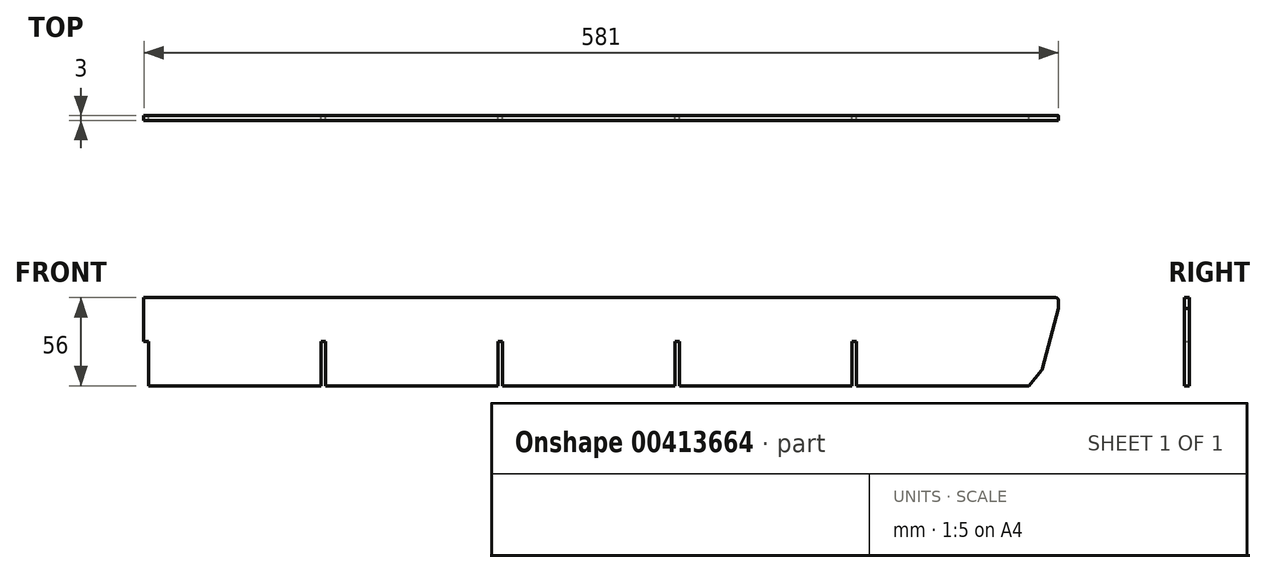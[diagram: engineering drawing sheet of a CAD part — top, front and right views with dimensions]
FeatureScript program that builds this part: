
annotation { "Feature Type Name" : "Feature", "Feature Type Description" : "" }
export const myFeature = defineFeature(function(context is Context, id is Id, definition is map)
    precondition{}
    {
        {
            var Q0;
            Q0=qCreatedBy(makeId("Front.planeOp"),FACE);
            var sketch = newSketch(context, id + "F0", { "sketchPlane" : qUnion([Q0])});
            skLineSegment(sketch, "E0.bottom", {"start": v(-12.6, -20.13) * mm, "end": v(-8.8, -20.13) * mm});
            skLineSegment(sketch, "E0.top", {"start": v(-12.6, 35.87) * mm, "end": v(345.4, 35.87) * mm});
            skLineSegment(sketch, "E0.right", {"start": v(347.4, 28.87) * mm, "end": v(347.4, 33.87) * mm});
            skArc(sketch, "E1", {"start": v(347.4, 33.87) * mm, "mid": v(346.82, 35.28) * mm, "end": v(345.4, 35.87) * mm});
            skLineSegment(sketch, "E2", {"start": v(328.4, -20.13) * mm, "end": v(336.6, -10.36) * mm});
            skPoint(sketch, "E3", {"position": v(347.4, 28.87) * mm});
            skLineSegment(sketch, "E4", {"start": v(347.4, 28.87) * mm, "end": v(337.2, -9.21) * mm});
            skArc(sketch, "E5", {"start": v(336.6, -10.36) * mm, "mid": v(336.97, -9.82) * mm, "end": v(337.2, -9.21) * mm});
            skLineSegment(sketch, "E6.MirrorCS", {"start": v(-12.6, 35.87) * mm, "end": v(-233.6, 35.87) * mm});
            skLineSegment(sketch, "E7.MirrorCS", {"start": v(-12.6, -20.13) * mm, "end": v(-118.2, -20.13) * mm});
            skPoint(sketch, "E8.orphan", {"position": v(347.4, -20.13) * mm});
            skLineSegment(sketch, "E9.top", {"start": v(216, 7.87) * mm, "end": v(219, 7.87) * mm});
            skLineSegment(sketch, "E9.left", {"start": v(216, -20.13) * mm, "end": v(216, 7.87) * mm});
            skLineSegment(sketch, "E9.right", {"start": v(219, -20.13) * mm, "end": v(219, 7.87) * mm});
            skLineSegment(sketch, "E10.bottom", {"start": v(-233.6, 7.87) * mm, "end": v(-230.6, 7.87) * mm});
            skLineSegment(sketch, "E10.left", {"start": v(-233.6, 7.87) * mm, "end": v(-233.6, -20.13) * mm});
            skLineSegment(sketch, "E10.right", {"start": v(-230.6, 7.87) * mm, "end": v(-230.6, -20.13) * mm});
            skLineSegment(sketch, "E11.bottom", {"start": v(103.6, 7.87) * mm, "end": v(106.6, 7.87) * mm});
            skLineSegment(sketch, "E11.left", {"start": v(103.6, 7.87) * mm, "end": v(103.6, -20.13) * mm});
            skLineSegment(sketch, "E11.right", {"start": v(106.6, 7.87) * mm, "end": v(106.6, -20.13) * mm});
            skLineSegment(sketch, "E12.bottom", {"start": v(-8.8, 7.87) * mm, "end": v(-5.8, 7.87) * mm});
            skLineSegment(sketch, "E12.left", {"start": v(-8.8, 7.87) * mm, "end": v(-8.8, -20.13) * mm});
            skLineSegment(sketch, "E12.right", {"start": v(-5.8, 7.87) * mm, "end": v(-5.8, -20.13) * mm});
            skLineSegment(sketch, "E13.bottom", {"start": v(-121.2, 7.87) * mm, "end": v(-118.2, 7.87) * mm});
            skLineSegment(sketch, "E13.left", {"start": v(-121.2, 7.87) * mm, "end": v(-121.2, -20.13) * mm});
            skLineSegment(sketch, "E13.right", {"start": v(-118.2, 7.87) * mm, "end": v(-118.2, -20.13) * mm});
            skLineSegment(sketch, "E14.trimOffspring", {"start": v(-121.2, -20.13) * mm, "end": v(-230.6, -20.13) * mm});
            skLineSegment(sketch, "E15.trimOffspring", {"start": v(-5.8, -20.13) * mm, "end": v(103.6, -20.13) * mm});
            skLineSegment(sketch, "E16.trimOffspring", {"start": v(106.6, -20.13) * mm, "end": v(216, -20.13) * mm});
            skLineSegment(sketch, "E17.trimOffspring", {"start": v(219, -20.13) * mm, "end": v(328.4, -20.13) * mm});
            skLineSegment(sketch, "E18", {"start": v(-233.6, 7.87) * mm, "end": v(-233.6, 35.87) * mm});
            skSolve(sketch);
        }
        {
            var Q0;
            Q0=makeQuery(id+"F0.imprint","IMPRINT",FACE,{"disambiguationData":[TD([[makeQuery(id+"F0.imprint","IMPRINT",EDGE,{"derivedFrom":sQuery(id+"F0.wireOp",EDGE,"E0.bottom")}),1.0]])]});
            extrude(context, id + "F1", {"entities" : qUnion([Q0]), "endBound" : BoundingType.SYMMETRIC, "depth" : 3 * mm});
        }
    });
